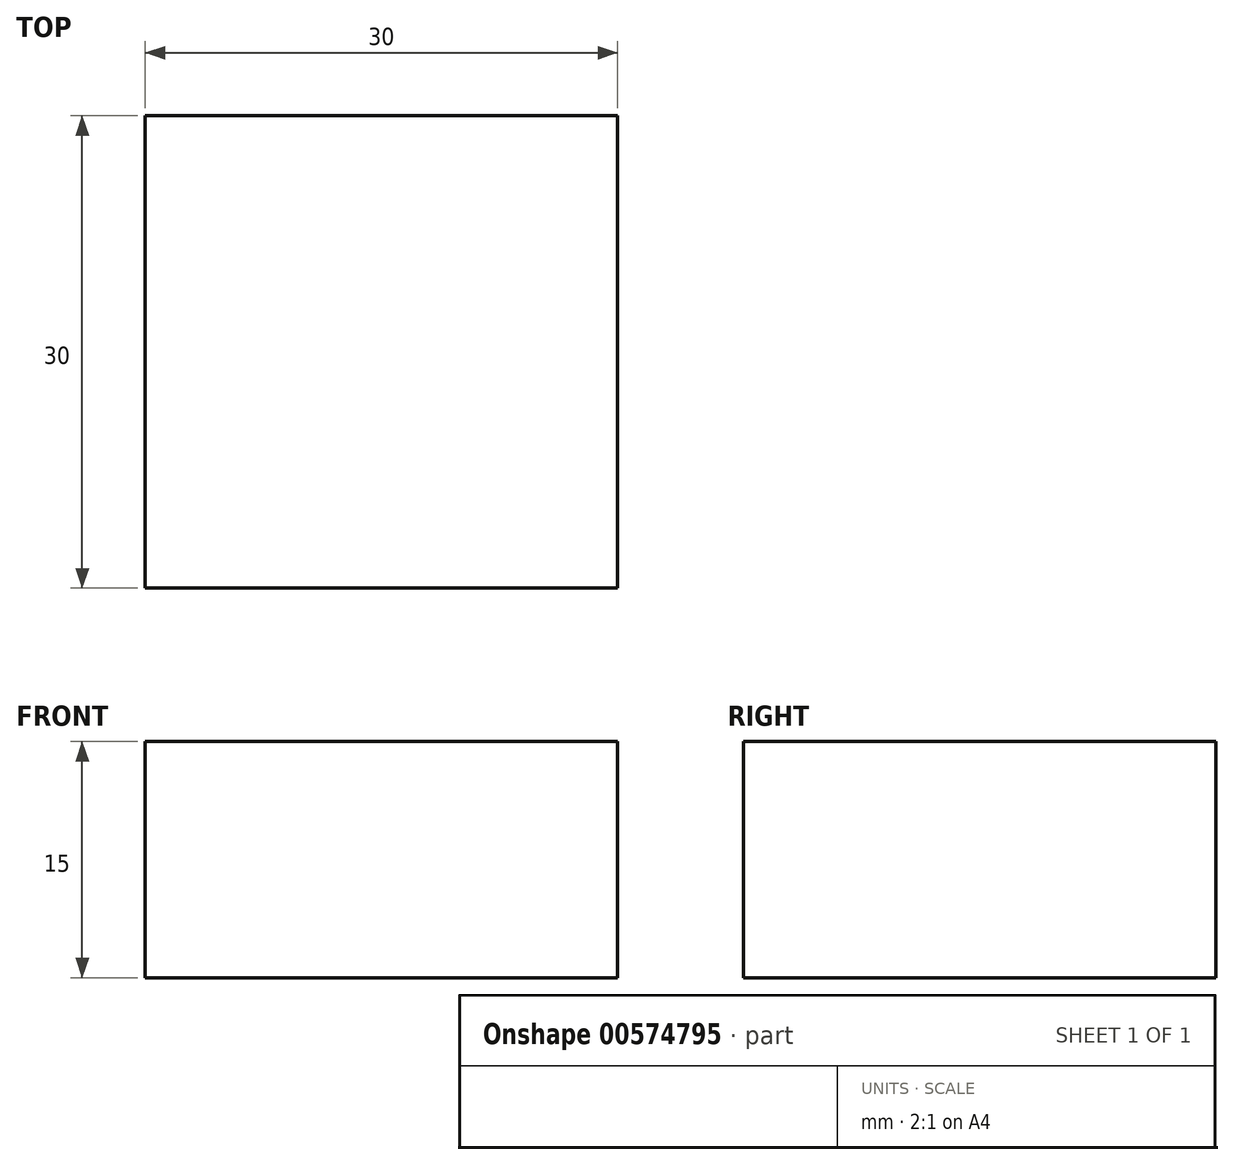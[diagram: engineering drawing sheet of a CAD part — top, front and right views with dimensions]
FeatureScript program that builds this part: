
annotation { "Feature Type Name" : "Feature", "Feature Type Description" : "" }
export const myFeature = defineFeature(function(context is Context, id is Id, definition is map)
    precondition{}
    {
        {
            var Q0;
            Q0=qCreatedBy(makeId("Top.planeOp"),FACE);
            var sketch = newSketch(context, id + "F0", { "sketchPlane" : qUnion([Q0])});
            skLineSegment(sketch, "E0.bottom", {"start": v(-15, -15) * mm, "end": v(15, -15) * mm});
            skLineSegment(sketch, "E0.top", {"start": v(-15, 15) * mm, "end": v(15, 15) * mm});
            skLineSegment(sketch, "E0.left", {"start": v(-15, -15) * mm, "end": v(-15, 15) * mm});
            skLineSegment(sketch, "E0.right", {"start": v(15, -15) * mm, "end": v(15, 15) * mm});
            skSolve(sketch);
        }
        {
            var Q0;
            Q0 = qSketchRegion(id + "F0", true);
            extrude(context, id + "F1", {"entities" : qUnion([Q0]), "depth" : 15 * mm, "offsetDistance" : 25 * mm});
        }
    });
